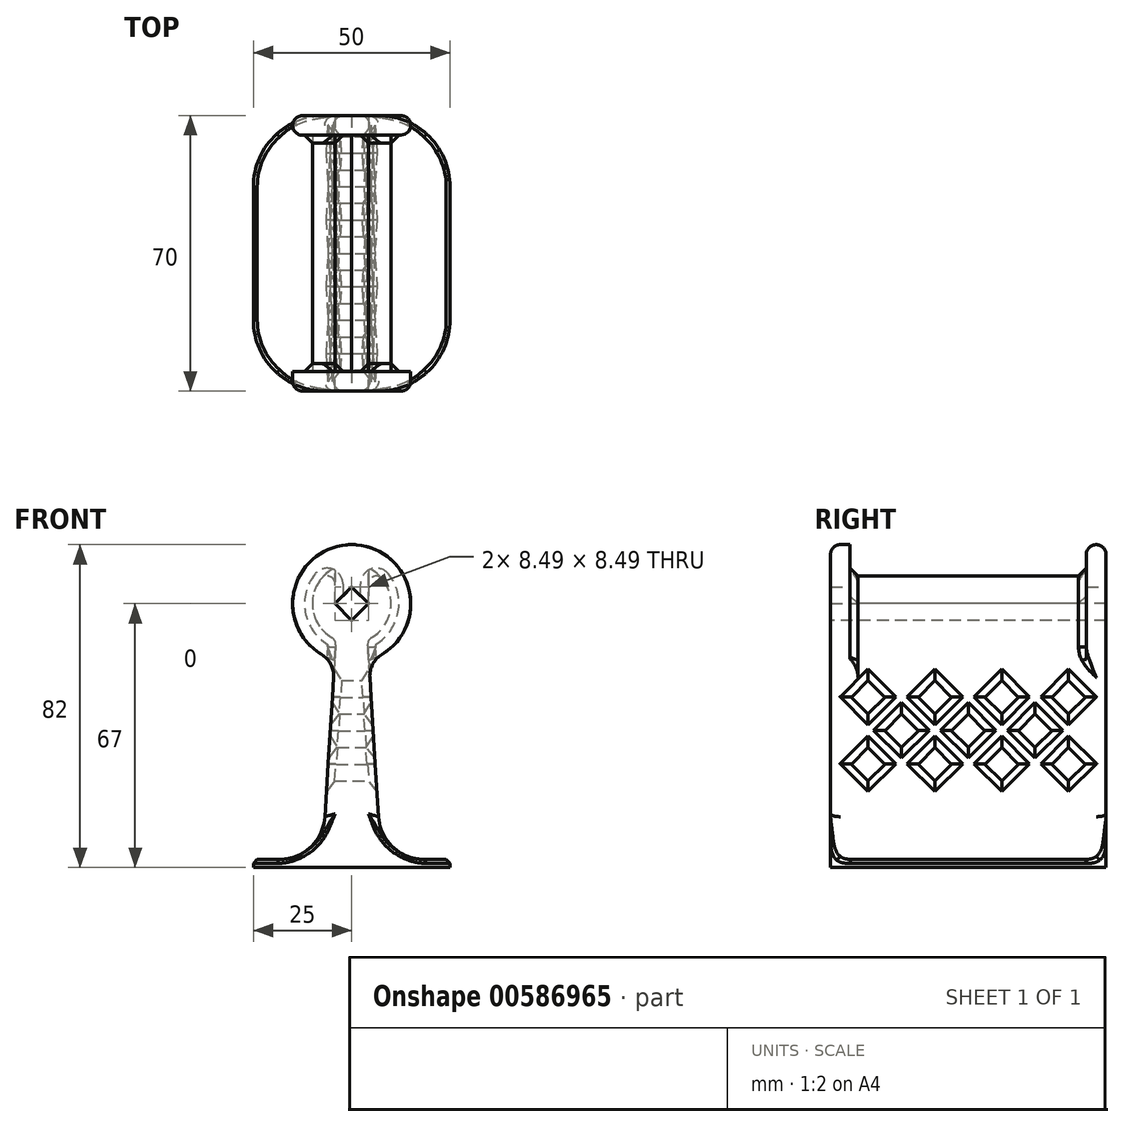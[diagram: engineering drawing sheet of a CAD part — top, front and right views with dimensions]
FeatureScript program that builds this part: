
annotation { "Feature Type Name" : "Feature", "Feature Type Description" : "" }
export const myFeature = defineFeature(function(context is Context, id is Id, definition is map)
    precondition{}
    {
        {
            var Q0;
            Q0=qCreatedBy(makeId("Front.planeOp"),FACE);
            var sketch = newSketch(context, id + "F0", { "sketchPlane" : qUnion([Q0])});
            skCircle(sketch, "E0", {"center": v(0, 0) * mm, "radius": 10 * mm});
            skCircle(sketch, "E1", {"center": v(0, 0) * mm, "radius": 15 * mm});
            skLineSegment(sketch, "E2.bottom", {"start": v(-25, -65) * mm, "end": v(25, -65) * mm});
            skLineSegment(sketch, "E2.top", {"start": v(-25, -67) * mm, "end": v(25, -67) * mm});
            skLineSegment(sketch, "E2.left", {"start": v(-25, -65) * mm, "end": v(-25, -67) * mm});
            skLineSegment(sketch, "E2.right", {"start": v(25, -65) * mm, "end": v(25, -67) * mm});
            skPoint(sketch, "E2.middle", {"position": v(0, -66) * mm});
            skLineSegment(sketch, "E3", {"start": v(-7.5, -65) * mm, "end": v(-4, -9.17) * mm});
            skLineSegment(sketch, "E4", {"start": v(7.5, -65) * mm, "end": v(4, -9.17) * mm});
            skPoint(sketch, "E5.orphan", {"position": v(-10, 0) * mm});
            skPoint(sketch, "E6.orphan", {"position": v(10, 0) * mm});
            skLineSegment(sketch, "E7", {"start": v(0, 0) * mm, "end": v(0, 10) * mm, "construction": true});
            skLineSegment(sketch, "E8", {"start": v(0, 4.24) * mm, "end": v(-4.24, 0) * mm});
            skLineSegment(sketch, "E9", {"start": v(-4.24, 0) * mm, "end": v(0, -4.24) * mm});
            skLineSegment(sketch, "E10", {"start": v(0, -4.24) * mm, "end": v(4.24, 0) * mm});
            skLineSegment(sketch, "E11", {"start": v(4.24, 0) * mm, "end": v(0, 4.24) * mm});
            skLineSegment(sketch, "E12", {"start": v(-4.24, 0) * mm, "end": v(-4.24, 9.06) * mm});
            skLineSegment(sketch, "E13", {"start": v(4.24, 0) * mm, "end": v(4.24, 9.06) * mm});
            skSolve(sketch);
        }
        {
            var Q0;
            Q0=makeQuery(id+"F0.imprint","IMPRINT",FACE,{"disambiguationData":[TD([[makeQuery(id+"F0.imprint","IMPRINT",EDGE,{"derivedFrom":sQuery(id+"F0.wireOp",EDGE,"E2.top")}),1.0]])]});
            var Q1;
            {var subQ0=sQuery(id+"F0.wireOp",EDGE,"E0");var subQ5=makeQuery(id+"F0.imprint","INTERSECT",VERTEX,{"derivedFrom":[subQ0,sQuery(id+"F0.wireOp",EDGE,"bGZqraN8-48Lf-gWye-19XN-i600Me7QwLsl")]});Q1=makeQuery(id+"F0.imprint","IMPRINT",FACE,{"disambiguationData":[TD([[makeQuery(id+"F0.imprint","IMPRINT",EDGE,{"disambiguationData":[TD([[subQ5,1.0]])],"derivedFrom":subQ0}),-1.0]])]});}
            var Q2;
            {var subQ0=sQuery(id+"F0.wireOp",EDGE,"5hKjGQrV-Ui9G-uASz-JZ0V-acZigOKFCtJ6");Q2=makeQuery(id+"F0.imprint","IMPRINT",FACE,{"disambiguationData":[TD([[makeQuery(id+"F0.imprint","IMPRINT",EDGE,{"derivedFrom":subQ0}),-1.0]])]});}
            var Q3;
            {var subQ1=sQuery(id+"F0.wireOp",EDGE,"bGZqraN8-48Lf-gWye-19XN-i600Me7QwLsl");Q3=makeQuery(id+"F0.imprint","IMPRINT",FACE,{"disambiguationData":[TD([[makeQuery(id+"F0.imprint","IMPRINT",EDGE,{"derivedFrom":subQ1}),1.0]])]});}
            var Q4;
            {var subQ0=sQuery(id+"F0.wireOp",EDGE,"bGZqraN8-48Lf-gWye-19XN-i600Me7QwLsl");Q4=makeQuery(id+"F0.imprint","IMPRINT",FACE,{"disambiguationData":[TD([[makeQuery(id+"F0.imprint","IMPRINT",EDGE,{"derivedFrom":subQ0}),-1.0]])]});}
            var Q5;
            {var subQ0=sQuery(id+"F0.wireOp",EDGE,"E3");Q5=makeQuery(id+"F0.imprint","IMPRINT",FACE,{"disambiguationData":[TD([[makeQuery(id+"F0.imprint","IMPRINT",EDGE,{"derivedFrom":subQ0}),-1.0]])]});}
            var Q6;
            {var subQ1=sQuery(id+"F0.wireOp",EDGE,"5hKjGQrV-Ui9G-uASz-JZ0V-acZigOKFCtJ6");Q6=makeQuery(id+"F0.imprint","IMPRINT",FACE,{"disambiguationData":[TD([[makeQuery(id+"F0.imprint","IMPRINT",EDGE,{"derivedFrom":subQ1}),1.0]])]});}
            var Q7;
            {var subQ0=sQuery(id+"F0.wireOp",EDGE,"FRuf11Uh-ZfHc-atdC-fj4W-Pp8RtlPbf5us");Q7=makeQuery(id+"F0.imprint","IMPRINT",FACE,{"disambiguationData":[TD([[makeQuery(id+"F0.imprint","IMPRINT",EDGE,{"derivedFrom":subQ0}),-1.0]])]});}
            var Q8;
            Q8=makeQuery(id+"F0.imprint","IMPRINT",FACE,{"disambiguationData":[TD([[makeQuery(id+"F0.imprint","IMPRINT",EDGE,{"derivedFrom":sQuery(id+"F0.wireOp",EDGE,"E8")}),-1.0]])]});
            var Q9;
            Q9=makeQuery(id+"F0.imprint","IMPRINT",FACE,{"disambiguationData":[TD([[makeQuery(id+"F0.imprint","IMPRINT",EDGE,{"derivedFrom":sQuery(id+"F0.wireOp",EDGE,"E8")}),1.0]])]});
            var Q10;
            Q10=makeQuery(id+"F0.imprint","IMPRINT",FACE,{"disambiguationData":[TD([[makeQuery(id+"F0.imprint","IMPRINT",EDGE,{"derivedFrom":sQuery(id+"F0.wireOp",EDGE,"E9")}),-1.0]])]});
            extrude(context, id + "F1", {"entities" : qUnion([Q0, Q1, Q2, Q3, Q4, Q5, Q6, Q7, Q8, Q9, Q10]), "endBound" : BoundingType.SYMMETRIC, "depth" : 70 * mm, "offsetDistance" : 25 * mm});
        }
        {
            var Q0;
            {var subQ1=sQuery(id+"F0.wireOp",EDGE,"E0");var subQ6=makeQuery(id+"F0.imprint","INTERSECT",VERTEX,{"derivedFrom":[subQ1,sQuery(id+"F0.wireOp",EDGE,"E12")]});Q0=makeQuery(id+"F0.imprint","IMPRINT",FACE,{"disambiguationData":[TD([[makeQuery(id+"F0.imprint","IMPRINT",EDGE,{"disambiguationData":[TD([[subQ6,1.0]])],"derivedFrom":subQ1}),-1.0]])]});}
            var Q1;
            Q1=makeQuery(id+"F0.imprint","IMPRINT",FACE,{"disambiguationData":[TD([[makeQuery(id+"F0.imprint","IMPRINT",EDGE,{"derivedFrom":sQuery(id+"F0.wireOp",EDGE,"E8")}),-1.0]])]});
            var Q2;
            Q2=makeQuery(id+"F0.imprint","IMPRINT",FACE,{"disambiguationData":[TD([[makeQuery(id+"F0.imprint","IMPRINT",EDGE,{"derivedFrom":sQuery(id+"F0.wireOp",EDGE,"E8")}),1.0]])]});
            extrude(context, id + "F2", {"entities" : qUnion([Q0, Q1, Q2]), "operationType" : NewBodyOperationType.REMOVE, "endBound" : BoundingType.SYMMETRIC, "oppositeDirection" : true, "depth" : 60 * mm, "offsetDistance" : 25 * mm});
        }
        {
            var Q0;
            Q0=makeQuery(id+"F0.imprint","IMPRINT",FACE,{"disambiguationData":[TD([[makeQuery(id+"F0.imprint","IMPRINT",EDGE,{"derivedFrom":sQuery(id+"F0.wireOp",EDGE,"E8")}),1.0]])]});
            extrude(context, id + "F3", {"entities" : qUnion([Q0]), "operationType" : NewBodyOperationType.REMOVE, "endBound" : BoundingType.SYMMETRIC, "depth" : 70 * mm, "offsetDistance" : 25 * mm});
        }
        {
            var Q0;
            Q0=makeQuery(id+"F1.opExtrude","CAP_EDGE",EDGE,{"disambiguationData":[OSD([sQuery(id+"F0.wireOp",EDGE,"E2.left")])],"isStart":true});
            var Q1;
            Q1=makeQuery(id+"F1.opExtrude","CAP_EDGE",EDGE,{"disambiguationData":[OSD([sQuery(id+"F0.wireOp",EDGE,"E2.left")])],"isStart":false});
            var Q2;
            Q2=makeQuery(id+"F1.opExtrude","CAP_EDGE",EDGE,{"disambiguationData":[OSD([sQuery(id+"F0.wireOp",EDGE,"E2.right")])],"isStart":true});
            var Q3;
            Q3=makeQuery(id+"F1.opExtrude","CAP_EDGE",EDGE,{"disambiguationData":[OSD([sQuery(id+"F0.wireOp",EDGE,"E2.right")])],"isStart":false});
            fillet(context, id + "F4", {"entities" : qUnion([Q0, Q1, Q2, Q3]), "radius" : 18.1 * mm, "tangentPropagation" : true, "allowEdgeOverflow" : false});
        }
        {
            var Q0;
            Q0=makeQuery(id+"F2.boolean.opBoolean","COPY",EDGE,{"derivedFrom":makeQuery(id+"F2.opExtrude","SWEPT_EDGE",EDGE,{"disambiguationData":[OSD([sQuery(id+"F0.wireOp",EDGE,"E0"),sQuery(id+"F0.wireOp",EDGE,"COAt9hvt-TYfE-I04l-2mVs-jGL3jd98xaqb")])]})});
            var Q1;
            Q1=makeQuery(id+"F2.boolean.opBoolean","COPY",EDGE,{"derivedFrom":makeQuery(id+"F2.opExtrude","SWEPT_EDGE",EDGE,{"disambiguationData":[OSD([sQuery(id+"F0.wireOp",EDGE,"E0"),sQuery(id+"F0.wireOp",EDGE,"bGZqraN8-48Lf-gWye-19XN-i600Me7QwLsl")])]})});
            var Q2;
            Q2=makeQuery(id+"F2.boolean.opBoolean","COPY",EDGE,{"derivedFrom":makeQuery(id+"F2.opExtrude","SWEPT_EDGE",EDGE,{"disambiguationData":[OSD([sQuery(id+"F0.wireOp",EDGE,"bGZqraN8-48Lf-gWye-19XN-i600Me7QwLsl"),sQuery(id+"F0.wireOp",EDGE,"COAt9hvt-TYfE-I04l-2mVs-jGL3jd98xaqb")])]})});
            fillet(context, id + "F5", {"entities" : qUnion([Q0, Q1, Q2]), "radius" : 2 * mm, "tangentPropagation" : true, "allowEdgeOverflow" : false});
        }
        {
            var Q0;
            Q0=makeQuery(id+"F2.boolean.opBoolean","COPY",EDGE,{"derivedFrom":makeQuery(id+"F2.opExtrude","SWEPT_EDGE",EDGE,{"disambiguationData":[OSD([sQuery(id+"F0.wireOp",EDGE,"E0"),sQuery(id+"F0.wireOp",EDGE,"E4")])]})});
            var Q1;
            {var subQ0=sQuery(id+"F0.wireOp",EDGE,"E4");var subQ1=sQuery(id+"F0.wireOp",EDGE,"E3");var subQ2=sQuery(id+"F0.wireOp",EDGE,"E1");Q1=makeQuery(id+"F2.boolean.opBoolean","SPLIT",EDGE,{"disambiguationData":[TD([makeQuery(id+"F2.opExtrude","CAP_FACE",FACE,{"disambiguationData":[OSD([sQuery(id+"F0.wireOp",EDGE,"E0"),subQ2,subQ1,subQ0,sQuery(id+"F0.wireOp",EDGE,"bGZqraN8-48Lf-gWye-19XN-i600Me7QwLsl"),sQuery(id+"F0.wireOp",EDGE,"COAt9hvt-TYfE-I04l-2mVs-jGL3jd98xaqb")])],"isStart":true})])],"derivedFrom":makeQuery(id+"F1.opExtrude","SWEPT_EDGE",EDGE,{"disambiguationData":[OSD([subQ2,subQ0])]})});}
            var Q2;
            {var subQ0=sQuery(id+"F0.wireOp",EDGE,"E3");var subQ1=sQuery(id+"F0.wireOp",EDGE,"E4");var subQ2=sQuery(id+"F0.wireOp",EDGE,"E1");Q2=makeQuery(id+"F2.boolean.opBoolean","SPLIT",EDGE,{"disambiguationData":[TD([makeQuery(id+"F2.opExtrude","CAP_FACE",FACE,{"disambiguationData":[OSD([sQuery(id+"F0.wireOp",EDGE,"E0"),subQ2,subQ0,subQ1,sQuery(id+"F0.wireOp",EDGE,"bGZqraN8-48Lf-gWye-19XN-i600Me7QwLsl"),sQuery(id+"F0.wireOp",EDGE,"COAt9hvt-TYfE-I04l-2mVs-jGL3jd98xaqb")])],"isStart":true})])],"derivedFrom":makeQuery(id+"F1.opExtrude","SWEPT_EDGE",EDGE,{"disambiguationData":[OSD([subQ2,subQ0])]})});}
            var Q3;
            Q3=makeQuery(id+"F2.boolean.opBoolean","COPY",EDGE,{"derivedFrom":makeQuery(id+"F2.opExtrude","SWEPT_EDGE",EDGE,{"disambiguationData":[OSD([sQuery(id+"F0.wireOp",EDGE,"E0"),sQuery(id+"F0.wireOp",EDGE,"E3")])]})});
            var Q4;
            {var subQ0=sQuery(id+"F0.wireOp",EDGE,"E4");var subQ1=sQuery(id+"F0.wireOp",EDGE,"E3");var subQ2=sQuery(id+"F0.wireOp",EDGE,"E1");Q4=makeQuery(id+"F2.boolean.opBoolean","SPLIT",EDGE,{"disambiguationData":[TD([makeQuery(id+"F2.opExtrude","CAP_FACE",FACE,{"disambiguationData":[OSD([sQuery(id+"F0.wireOp",EDGE,"E0"),subQ2,subQ1,subQ0,sQuery(id+"F0.wireOp",EDGE,"bGZqraN8-48Lf-gWye-19XN-i600Me7QwLsl"),sQuery(id+"F0.wireOp",EDGE,"COAt9hvt-TYfE-I04l-2mVs-jGL3jd98xaqb")])],"isStart":false})])],"derivedFrom":makeQuery(id+"F1.opExtrude","SWEPT_EDGE",EDGE,{"disambiguationData":[OSD([subQ2,subQ0])]})});}
            var Q5;
            {var subQ0=sQuery(id+"F0.wireOp",EDGE,"E4");var subQ1=sQuery(id+"F0.wireOp",EDGE,"E3");var subQ2=sQuery(id+"F0.wireOp",EDGE,"E1");Q5=makeQuery(id+"F2.boolean.opBoolean","SPLIT",EDGE,{"disambiguationData":[TD([makeQuery(id+"F2.opExtrude","CAP_FACE",FACE,{"disambiguationData":[OSD([sQuery(id+"F0.wireOp",EDGE,"E0"),subQ2,subQ1,subQ0,sQuery(id+"F0.wireOp",EDGE,"bGZqraN8-48Lf-gWye-19XN-i600Me7QwLsl"),sQuery(id+"F0.wireOp",EDGE,"COAt9hvt-TYfE-I04l-2mVs-jGL3jd98xaqb")])],"isStart":false})])],"derivedFrom":makeQuery(id+"F1.opExtrude","SWEPT_EDGE",EDGE,{"disambiguationData":[OSD([subQ2,subQ1])]})});}
            fillet(context, id + "F6", {"entities" : qUnion([Q0, Q1, Q2, Q3, Q4, Q5]), "radius" : 6.43 * mm, "tangentPropagation" : true, "allowEdgeOverflow" : false});
        }
        {
            var Q0;
            Q0=makeQuery(id+"F1.opExtrude","CAP_EDGE",EDGE,{"disambiguationData":[OSD([sQuery(id+"F0.wireOp",EDGE,"E1")])],"isStart":false});
            var Q1;
            Q1=makeQuery(id+"F1.opExtrude","CAP_EDGE",EDGE,{"disambiguationData":[OSD([sQuery(id+"F0.wireOp",EDGE,"E1")])],"isStart":true});
            var Q2;
            Q2=makeQuery(id+"F2.boolean.opBoolean","COPY",EDGE,{"derivedFrom":makeQuery(id+"F2.opExtrude","CAP_EDGE",EDGE,{"disambiguationData":[OSD([sQuery(id+"F0.wireOp",EDGE,"E1")])],"isStart":false})});
            var Q3;
            Q3=makeQuery(id+"F2.boolean.opBoolean","COPY",EDGE,{"derivedFrom":makeQuery(id+"F2.opExtrude","CAP_EDGE",EDGE,{"disambiguationData":[OSD([sQuery(id+"F0.wireOp",EDGE,"E1")])],"isStart":true})});
            fillet(context, id + "F7", {"entities" : qUnion([Q0, Q1, Q2, Q3]), "radius" : 2.5 * mm, "tangentPropagation" : true, "allowEdgeOverflow" : false});
        }
        {
            var Q0;
            Q0=makeQuery(id+"F1.opExtrude","SWEPT_EDGE",EDGE,{"disambiguationData":[OSD([sQuery(id+"F0.wireOp",EDGE,"E2.bottom"),sQuery(id+"F0.wireOp",EDGE,"E3")])]});
            var Q1;
            Q1=makeQuery(id+"F1.opExtrude","SWEPT_EDGE",EDGE,{"disambiguationData":[OSD([sQuery(id+"F0.wireOp",EDGE,"E2.bottom"),sQuery(id+"F0.wireOp",EDGE,"E4")])]});
            fillet(context, id + "F8", {"entities" : qUnion([Q0, Q1]), "radius" : 11.6 * mm, "tangentPropagation" : true, "allowEdgeOverflow" : false});
        }
        {
            var Q0;
            Q0=makeQuery(id+"F1.opExtrude","SWEPT_EDGE",EDGE,{"disambiguationData":[OSD([sQuery(id+"F0.wireOp",EDGE,"E2.bottom"),sQuery(id+"F0.wireOp",EDGE,"E2.right")])]});
            var Q1;
            Q1=makeQuery(id+"F1.opExtrude","SWEPT_EDGE",EDGE,{"disambiguationData":[OSD([sQuery(id+"F0.wireOp",EDGE,"E2.bottom"),sQuery(id+"F0.wireOp",EDGE,"E2.left")])]});
            chamfer(context, id + "F9", {"entities" : qUnion([Q0, Q1]), "width" : 1 * mm, "tangentPropagation" : true});
        }
        {
            var Q0;
            Q0=qCreatedBy(makeId("Right.planeOp"),FACE);
            var sketch = newSketch(context, id + "F10", { "sketchPlane" : qUnion([Q0])});
            skLineSegment(sketch, "E14", {"start": v(-25.46, -36.55) * mm, "end": v(-29.7, -40.79) * mm});
            skLineSegment(sketch, "E15", {"start": v(-29.7, -40.79) * mm, "end": v(-25.46, -45.03) * mm});
            skLineSegment(sketch, "E16", {"start": v(-25.46, -45.03) * mm, "end": v(-21.21, -40.79) * mm});
            skLineSegment(sketch, "E17", {"start": v(-21.21, -40.79) * mm, "end": v(-25.46, -36.55) * mm});
            skLineSegment(sketch, "E18.0.1.0", {"start": v(-21.21, -23.82) * mm, "end": v(-25.46, -19.58) * mm});
            skLineSegment(sketch, "E18.0.1.1", {"start": v(-25.46, -19.58) * mm, "end": v(-29.7, -23.82) * mm});
            skLineSegment(sketch, "E18.0.1.2", {"start": v(-29.7, -23.82) * mm, "end": v(-25.46, -28.06) * mm});
            skLineSegment(sketch, "E18.0.1.3", {"start": v(-25.46, -28.06) * mm, "end": v(-21.21, -23.82) * mm});
            skLineSegment(sketch, "E18.1.0.0", {"start": v(-12.73, -49.27) * mm, "end": v(-16.97, -45.03) * mm});
            skLineSegment(sketch, "E18.1.0.1", {"start": v(-16.97, -45.03) * mm, "end": v(-21.21, -49.27) * mm});
            skLineSegment(sketch, "E18.1.0.2", {"start": v(-21.21, -49.27) * mm, "end": v(-16.97, -53.52) * mm});
            skLineSegment(sketch, "E18.1.0.3", {"start": v(-16.97, -53.52) * mm, "end": v(-12.73, -49.27) * mm});
            skLineSegment(sketch, "E18.1.1.0", {"start": v(-12.73, -32.3) * mm, "end": v(-16.97, -28.06) * mm});
            skLineSegment(sketch, "E18.1.1.1", {"start": v(-16.97, -28.06) * mm, "end": v(-21.21, -32.3) * mm});
            skLineSegment(sketch, "E18.1.1.2", {"start": v(-21.21, -32.3) * mm, "end": v(-16.97, -36.55) * mm});
            skLineSegment(sketch, "E18.1.1.3", {"start": v(-16.97, -36.55) * mm, "end": v(-12.73, -32.3) * mm});
            skLineSegment(sketch, "E18.2.0.0", {"start": v(-4.24, -57.76) * mm, "end": v(-8.49, -53.52) * mm});
            skLineSegment(sketch, "E18.2.0.1", {"start": v(-8.49, -53.52) * mm, "end": v(-12.73, -57.76) * mm});
            skLineSegment(sketch, "E18.2.0.2", {"start": v(-12.73, -57.76) * mm, "end": v(-8.49, -62) * mm});
            skLineSegment(sketch, "E18.2.0.3", {"start": v(-8.49, -62) * mm, "end": v(-4.24, -57.76) * mm});
            skLineSegment(sketch, "E18.2.1.0", {"start": v(-4.24, -40.79) * mm, "end": v(-8.49, -36.55) * mm});
            skLineSegment(sketch, "E18.2.1.1", {"start": v(-8.49, -36.55) * mm, "end": v(-12.73, -40.79) * mm});
            skLineSegment(sketch, "E18.2.1.2", {"start": v(-12.73, -40.79) * mm, "end": v(-8.49, -45.03) * mm});
            skLineSegment(sketch, "E18.2.1.3", {"start": v(-8.49, -45.03) * mm, "end": v(-4.24, -40.79) * mm});
            skLineSegment(sketch, "E18.direction1", {"start": v(-29.7, -40.79) * mm, "end": v(-21.21, -49.27) * mm, "construction": true});
            skLineSegment(sketch, "E18.direction2", {"start": v(-29.7, -40.79) * mm, "end": v(-29.7, -23.82) * mm, "construction": true});
            skLineSegment(sketch, "E19.0.3.0", {"start": v(4.24, -66.25) * mm, "end": v(0, -62) * mm});
            skLineSegment(sketch, "E19.3.3.0", {"start": v(0, -62) * mm, "end": v(-4.24, -66.25) * mm});
            skLineSegment(sketch, "E19.6.3.0", {"start": v(-4.24, -66.25) * mm, "end": v(0, -70.49) * mm});
            skLineSegment(sketch, "E19.9.3.0", {"start": v(0, -70.49) * mm, "end": v(4.24, -66.25) * mm});
            skLineSegment(sketch, "E19.0.3.1", {"start": v(4.24, -49.27) * mm, "end": v(0, -45.03) * mm});
            skLineSegment(sketch, "E19.3.3.1", {"start": v(0, -45.03) * mm, "end": v(-4.24, -49.27) * mm});
            skLineSegment(sketch, "E19.6.3.1", {"start": v(-4.24, -49.27) * mm, "end": v(0, -53.52) * mm});
            skLineSegment(sketch, "E19.9.3.1", {"start": v(0, -53.52) * mm, "end": v(4.24, -49.27) * mm});
            skLineSegment(sketch, "E20.0.0.2", {"start": v(-21.21, -6.85) * mm, "end": v(-25.46, -2.6) * mm});
            skLineSegment(sketch, "E20.3.0.2", {"start": v(-25.46, -2.6) * mm, "end": v(-29.7, -6.85) * mm});
            skLineSegment(sketch, "E20.6.0.2", {"start": v(-29.7, -6.85) * mm, "end": v(-25.46, -11.1) * mm});
            skLineSegment(sketch, "E20.9.0.2", {"start": v(-25.46, -11.1) * mm, "end": v(-21.21, -6.85) * mm});
            skLineSegment(sketch, "E20.0.0.3", {"start": v(-21.21, 10.12) * mm, "end": v(-25.46, 14.36) * mm});
            skLineSegment(sketch, "E20.3.0.3", {"start": v(-25.46, 14.36) * mm, "end": v(-29.7, 10.12) * mm});
            skLineSegment(sketch, "E20.6.0.3", {"start": v(-29.7, 10.12) * mm, "end": v(-25.46, 5.88) * mm});
            skLineSegment(sketch, "E20.9.0.3", {"start": v(-25.46, 5.88) * mm, "end": v(-21.21, 10.12) * mm});
            skLineSegment(sketch, "E20.0.0.4", {"start": v(-21.21, 27.1) * mm, "end": v(-25.46, 31.34) * mm});
            skLineSegment(sketch, "E20.3.0.4", {"start": v(-25.46, 31.34) * mm, "end": v(-29.7, 27.1) * mm});
            skLineSegment(sketch, "E20.6.0.4", {"start": v(-29.7, 27.1) * mm, "end": v(-25.46, 22.85) * mm});
            skLineSegment(sketch, "E20.9.0.4", {"start": v(-25.46, 22.85) * mm, "end": v(-21.21, 27.1) * mm});
            skLineSegment(sketch, "E20.0.0.5", {"start": v(-21.21, 44.06) * mm, "end": v(-25.46, 48.3) * mm});
            skLineSegment(sketch, "E20.3.0.5", {"start": v(-25.46, 48.3) * mm, "end": v(-29.7, 44.06) * mm});
            skLineSegment(sketch, "E20.6.0.5", {"start": v(-29.7, 44.06) * mm, "end": v(-25.46, 39.82) * mm});
            skLineSegment(sketch, "E20.9.0.5", {"start": v(-25.46, 39.82) * mm, "end": v(-21.21, 44.06) * mm});
            skLineSegment(sketch, "E20.0.1.2", {"start": v(-12.73, -15.33) * mm, "end": v(-16.97, -11.1) * mm});
            skLineSegment(sketch, "E20.3.1.2", {"start": v(-16.97, -11.1) * mm, "end": v(-21.21, -15.33) * mm});
            skLineSegment(sketch, "E20.6.1.2", {"start": v(-21.21, -15.33) * mm, "end": v(-16.97, -19.58) * mm});
            skLineSegment(sketch, "E20.9.1.2", {"start": v(-16.97, -19.58) * mm, "end": v(-12.73, -15.33) * mm});
            skLineSegment(sketch, "E20.0.1.3", {"start": v(-12.73, 1.64) * mm, "end": v(-16.97, 5.88) * mm});
            skLineSegment(sketch, "E20.3.1.3", {"start": v(-16.97, 5.88) * mm, "end": v(-21.21, 1.64) * mm});
            skLineSegment(sketch, "E20.6.1.3", {"start": v(-21.21, 1.64) * mm, "end": v(-16.97, -2.6) * mm});
            skLineSegment(sketch, "E20.9.1.3", {"start": v(-16.97, -2.6) * mm, "end": v(-12.73, 1.64) * mm});
            skLineSegment(sketch, "E20.0.1.4", {"start": v(-12.73, 18.6) * mm, "end": v(-16.97, 22.85) * mm});
            skLineSegment(sketch, "E20.3.1.4", {"start": v(-16.97, 22.85) * mm, "end": v(-21.21, 18.6) * mm});
            skLineSegment(sketch, "E20.6.1.4", {"start": v(-21.21, 18.6) * mm, "end": v(-16.97, 14.36) * mm});
            skLineSegment(sketch, "E20.9.1.4", {"start": v(-16.97, 14.36) * mm, "end": v(-12.73, 18.6) * mm});
            skLineSegment(sketch, "E20.0.1.5", {"start": v(-12.73, 35.58) * mm, "end": v(-16.97, 39.82) * mm});
            skLineSegment(sketch, "E20.3.1.5", {"start": v(-16.97, 39.82) * mm, "end": v(-21.21, 35.58) * mm});
            skLineSegment(sketch, "E20.6.1.5", {"start": v(-21.21, 35.58) * mm, "end": v(-16.97, 31.34) * mm});
            skLineSegment(sketch, "E20.9.1.5", {"start": v(-16.97, 31.34) * mm, "end": v(-12.73, 35.58) * mm});
            skLineSegment(sketch, "E20.0.2.2", {"start": v(-4.24, -23.82) * mm, "end": v(-8.49, -19.58) * mm});
            skLineSegment(sketch, "E20.3.2.2", {"start": v(-8.49, -19.58) * mm, "end": v(-12.73, -23.82) * mm});
            skLineSegment(sketch, "E20.6.2.2", {"start": v(-12.73, -23.82) * mm, "end": v(-8.49, -28.06) * mm});
            skLineSegment(sketch, "E20.9.2.2", {"start": v(-8.49, -28.06) * mm, "end": v(-4.24, -23.82) * mm});
            skLineSegment(sketch, "E20.0.2.3", {"start": v(-4.24, -6.85) * mm, "end": v(-8.49, -2.6) * mm});
            skLineSegment(sketch, "E20.3.2.3", {"start": v(-8.49, -2.6) * mm, "end": v(-12.73, -6.85) * mm});
            skLineSegment(sketch, "E20.6.2.3", {"start": v(-12.73, -6.85) * mm, "end": v(-8.49, -11.1) * mm});
            skLineSegment(sketch, "E20.9.2.3", {"start": v(-8.49, -11.1) * mm, "end": v(-4.24, -6.85) * mm});
            skLineSegment(sketch, "E20.0.2.4", {"start": v(-4.24, 10.12) * mm, "end": v(-8.49, 14.36) * mm});
            skLineSegment(sketch, "E20.3.2.4", {"start": v(-8.49, 14.36) * mm, "end": v(-12.73, 10.12) * mm});
            skLineSegment(sketch, "E20.6.2.4", {"start": v(-12.73, 10.12) * mm, "end": v(-8.49, 5.88) * mm});
            skLineSegment(sketch, "E20.9.2.4", {"start": v(-8.49, 5.88) * mm, "end": v(-4.24, 10.12) * mm});
            skLineSegment(sketch, "E20.0.2.5", {"start": v(-4.24, 27.1) * mm, "end": v(-8.49, 31.34) * mm});
            skLineSegment(sketch, "E20.3.2.5", {"start": v(-8.49, 31.34) * mm, "end": v(-12.73, 27.1) * mm});
            skLineSegment(sketch, "E20.6.2.5", {"start": v(-12.73, 27.1) * mm, "end": v(-8.49, 22.85) * mm});
            skLineSegment(sketch, "E20.9.2.5", {"start": v(-8.49, 22.85) * mm, "end": v(-4.24, 27.1) * mm});
            skLineSegment(sketch, "E20.0.3.2", {"start": v(4.24, -32.3) * mm, "end": v(0, -28.06) * mm});
            skLineSegment(sketch, "E20.3.3.2", {"start": v(0, -28.06) * mm, "end": v(-4.24, -32.3) * mm});
            skLineSegment(sketch, "E20.6.3.2", {"start": v(-4.24, -32.3) * mm, "end": v(0, -36.55) * mm});
            skLineSegment(sketch, "E20.9.3.2", {"start": v(0, -36.55) * mm, "end": v(4.24, -32.3) * mm});
            skLineSegment(sketch, "E20.0.3.3", {"start": v(4.24, -15.33) * mm, "end": v(0, -11.1) * mm});
            skLineSegment(sketch, "E20.3.3.3", {"start": v(0, -11.1) * mm, "end": v(-4.24, -15.33) * mm});
            skLineSegment(sketch, "E20.6.3.3", {"start": v(-4.24, -15.33) * mm, "end": v(0, -19.58) * mm});
            skLineSegment(sketch, "E20.9.3.3", {"start": v(0, -19.58) * mm, "end": v(4.24, -15.33) * mm});
            skLineSegment(sketch, "E20.0.3.4", {"start": v(4.24, 1.64) * mm, "end": v(0, 5.88) * mm});
            skLineSegment(sketch, "E20.3.3.4", {"start": v(0, 5.88) * mm, "end": v(-4.24, 1.64) * mm});
            skLineSegment(sketch, "E20.6.3.4", {"start": v(-4.24, 1.64) * mm, "end": v(0, -2.6) * mm});
            skLineSegment(sketch, "E20.9.3.4", {"start": v(0, -2.6) * mm, "end": v(4.24, 1.64) * mm});
            skLineSegment(sketch, "E20.0.3.5", {"start": v(4.24, 18.6) * mm, "end": v(0, 22.85) * mm});
            skLineSegment(sketch, "E20.3.3.5", {"start": v(0, 22.85) * mm, "end": v(-4.24, 18.6) * mm});
            skLineSegment(sketch, "E20.6.3.5", {"start": v(-4.24, 18.6) * mm, "end": v(0, 14.36) * mm});
            skLineSegment(sketch, "E20.9.3.5", {"start": v(0, 14.36) * mm, "end": v(4.24, 18.6) * mm});
            skLineSegment(sketch, "E21.0.4.0", {"start": v(12.73, -74.73) * mm, "end": v(8.49, -70.49) * mm});
            skLineSegment(sketch, "E21.3.4.0", {"start": v(8.49, -70.49) * mm, "end": v(4.24, -74.73) * mm});
            skLineSegment(sketch, "E21.6.4.0", {"start": v(4.24, -74.73) * mm, "end": v(8.49, -78.97) * mm});
            skLineSegment(sketch, "E21.9.4.0", {"start": v(8.49, -78.97) * mm, "end": v(12.73, -74.73) * mm});
            skLineSegment(sketch, "E21.0.4.1", {"start": v(12.73, -57.76) * mm, "end": v(8.49, -53.52) * mm});
            skLineSegment(sketch, "E21.3.4.1", {"start": v(8.49, -53.52) * mm, "end": v(4.24, -57.76) * mm});
            skLineSegment(sketch, "E21.6.4.1", {"start": v(4.24, -57.76) * mm, "end": v(8.49, -62) * mm});
            skLineSegment(sketch, "E21.9.4.1", {"start": v(8.49, -62) * mm, "end": v(12.73, -57.76) * mm});
            skLineSegment(sketch, "E21.0.4.2", {"start": v(12.73, -40.79) * mm, "end": v(8.49, -36.55) * mm});
            skLineSegment(sketch, "E21.3.4.2", {"start": v(8.49, -36.55) * mm, "end": v(4.24, -40.79) * mm});
            skLineSegment(sketch, "E21.6.4.2", {"start": v(4.24, -40.79) * mm, "end": v(8.49, -45.03) * mm});
            skLineSegment(sketch, "E21.9.4.2", {"start": v(8.49, -45.03) * mm, "end": v(12.73, -40.79) * mm});
            skLineSegment(sketch, "E21.0.4.3", {"start": v(12.73, -23.82) * mm, "end": v(8.49, -19.58) * mm});
            skLineSegment(sketch, "E21.3.4.3", {"start": v(8.49, -19.58) * mm, "end": v(4.24, -23.82) * mm});
            skLineSegment(sketch, "E21.6.4.3", {"start": v(4.24, -23.82) * mm, "end": v(8.49, -28.06) * mm});
            skLineSegment(sketch, "E21.9.4.3", {"start": v(8.49, -28.06) * mm, "end": v(12.73, -23.82) * mm});
            skLineSegment(sketch, "E21.0.4.4", {"start": v(12.73, -6.85) * mm, "end": v(8.49, -2.6) * mm});
            skLineSegment(sketch, "E21.3.4.4", {"start": v(8.49, -2.6) * mm, "end": v(4.24, -6.85) * mm});
            skLineSegment(sketch, "E21.6.4.4", {"start": v(4.24, -6.85) * mm, "end": v(8.49, -11.1) * mm});
            skLineSegment(sketch, "E21.9.4.4", {"start": v(8.49, -11.1) * mm, "end": v(12.73, -6.85) * mm});
            skLineSegment(sketch, "E21.0.4.5", {"start": v(12.73, 10.12) * mm, "end": v(8.49, 14.36) * mm});
            skLineSegment(sketch, "E21.3.4.5", {"start": v(8.49, 14.36) * mm, "end": v(4.24, 10.12) * mm});
            skLineSegment(sketch, "E21.6.4.5", {"start": v(4.24, 10.12) * mm, "end": v(8.49, 5.88) * mm});
            skLineSegment(sketch, "E21.9.4.5", {"start": v(8.49, 5.88) * mm, "end": v(12.73, 10.12) * mm});
            skLineSegment(sketch, "E21.0.5.0", {"start": v(21.21, -83.22) * mm, "end": v(16.97, -78.97) * mm});
            skLineSegment(sketch, "E21.3.5.0", {"start": v(16.97, -78.97) * mm, "end": v(12.73, -83.22) * mm});
            skLineSegment(sketch, "E21.6.5.0", {"start": v(12.73, -83.22) * mm, "end": v(16.97, -87.46) * mm});
            skLineSegment(sketch, "E21.9.5.0", {"start": v(16.97, -87.46) * mm, "end": v(21.21, -83.22) * mm});
            skLineSegment(sketch, "E21.0.5.1", {"start": v(21.21, -66.25) * mm, "end": v(16.97, -62) * mm});
            skLineSegment(sketch, "E21.3.5.1", {"start": v(16.97, -62) * mm, "end": v(12.73, -66.25) * mm});
            skLineSegment(sketch, "E21.6.5.1", {"start": v(12.73, -66.25) * mm, "end": v(16.97, -70.49) * mm});
            skLineSegment(sketch, "E21.9.5.1", {"start": v(16.97, -70.49) * mm, "end": v(21.21, -66.25) * mm});
            skLineSegment(sketch, "E21.0.5.2", {"start": v(21.21, -49.27) * mm, "end": v(16.97, -45.03) * mm});
            skLineSegment(sketch, "E21.3.5.2", {"start": v(16.97, -45.03) * mm, "end": v(12.73, -49.27) * mm});
            skLineSegment(sketch, "E21.6.5.2", {"start": v(12.73, -49.27) * mm, "end": v(16.97, -53.52) * mm});
            skLineSegment(sketch, "E21.9.5.2", {"start": v(16.97, -53.52) * mm, "end": v(21.21, -49.27) * mm});
            skLineSegment(sketch, "E21.0.5.3", {"start": v(21.21, -32.3) * mm, "end": v(16.97, -28.06) * mm});
            skLineSegment(sketch, "E21.3.5.3", {"start": v(16.97, -28.06) * mm, "end": v(12.73, -32.3) * mm});
            skLineSegment(sketch, "E21.6.5.3", {"start": v(12.73, -32.3) * mm, "end": v(16.97, -36.55) * mm});
            skLineSegment(sketch, "E21.9.5.3", {"start": v(16.97, -36.55) * mm, "end": v(21.21, -32.3) * mm});
            skLineSegment(sketch, "E21.0.5.4", {"start": v(21.21, -15.33) * mm, "end": v(16.97, -11.1) * mm});
            skLineSegment(sketch, "E21.3.5.4", {"start": v(16.97, -11.1) * mm, "end": v(12.73, -15.33) * mm});
            skLineSegment(sketch, "E21.6.5.4", {"start": v(12.73, -15.33) * mm, "end": v(16.97, -19.58) * mm});
            skLineSegment(sketch, "E21.9.5.4", {"start": v(16.97, -19.58) * mm, "end": v(21.21, -15.33) * mm});
            skLineSegment(sketch, "E21.0.5.5", {"start": v(21.21, 1.64) * mm, "end": v(16.97, 5.88) * mm});
            skLineSegment(sketch, "E21.3.5.5", {"start": v(16.97, 5.88) * mm, "end": v(12.73, 1.64) * mm});
            skLineSegment(sketch, "E21.6.5.5", {"start": v(12.73, 1.64) * mm, "end": v(16.97, -2.6) * mm});
            skLineSegment(sketch, "E21.9.5.5", {"start": v(16.97, -2.6) * mm, "end": v(21.21, 1.64) * mm});
            skLineSegment(sketch, "E21.0.6.0", {"start": v(29.7, -91.7) * mm, "end": v(25.46, -87.46) * mm});
            skLineSegment(sketch, "E21.3.6.0", {"start": v(25.46, -87.46) * mm, "end": v(21.21, -91.7) * mm});
            skLineSegment(sketch, "E21.6.6.0", {"start": v(21.21, -91.7) * mm, "end": v(25.46, -95.94) * mm});
            skLineSegment(sketch, "E21.9.6.0", {"start": v(25.46, -95.94) * mm, "end": v(29.7, -91.7) * mm});
            skLineSegment(sketch, "E21.0.6.1", {"start": v(29.7, -74.73) * mm, "end": v(25.46, -70.49) * mm});
            skLineSegment(sketch, "E21.3.6.1", {"start": v(25.46, -70.49) * mm, "end": v(21.21, -74.73) * mm});
            skLineSegment(sketch, "E21.6.6.1", {"start": v(21.21, -74.73) * mm, "end": v(25.46, -78.97) * mm});
            skLineSegment(sketch, "E21.9.6.1", {"start": v(25.46, -78.97) * mm, "end": v(29.7, -74.73) * mm});
            skLineSegment(sketch, "E21.0.6.2", {"start": v(29.7, -57.76) * mm, "end": v(25.46, -53.52) * mm});
            skLineSegment(sketch, "E21.3.6.2", {"start": v(25.46, -53.52) * mm, "end": v(21.21, -57.76) * mm});
            skLineSegment(sketch, "E21.6.6.2", {"start": v(21.21, -57.76) * mm, "end": v(25.46, -62) * mm});
            skLineSegment(sketch, "E21.9.6.2", {"start": v(25.46, -62) * mm, "end": v(29.7, -57.76) * mm});
            skLineSegment(sketch, "E21.0.6.3", {"start": v(29.7, -40.79) * mm, "end": v(25.46, -36.55) * mm});
            skLineSegment(sketch, "E21.3.6.3", {"start": v(25.46, -36.55) * mm, "end": v(21.21, -40.79) * mm});
            skLineSegment(sketch, "E21.6.6.3", {"start": v(21.21, -40.79) * mm, "end": v(25.46, -45.03) * mm});
            skLineSegment(sketch, "E21.9.6.3", {"start": v(25.46, -45.03) * mm, "end": v(29.7, -40.79) * mm});
            skLineSegment(sketch, "E21.0.6.4", {"start": v(29.7, -23.82) * mm, "end": v(25.46, -19.58) * mm});
            skLineSegment(sketch, "E21.3.6.4", {"start": v(25.46, -19.58) * mm, "end": v(21.21, -23.82) * mm});
            skLineSegment(sketch, "E21.6.6.4", {"start": v(21.21, -23.82) * mm, "end": v(25.46, -28.06) * mm});
            skLineSegment(sketch, "E21.9.6.4", {"start": v(25.46, -28.06) * mm, "end": v(29.7, -23.82) * mm});
            skLineSegment(sketch, "E21.0.6.5", {"start": v(29.7, -6.85) * mm, "end": v(25.46, -2.6) * mm});
            skLineSegment(sketch, "E21.3.6.5", {"start": v(25.46, -2.6) * mm, "end": v(21.21, -6.85) * mm});
            skLineSegment(sketch, "E21.6.6.5", {"start": v(21.21, -6.85) * mm, "end": v(25.46, -11.1) * mm});
            skLineSegment(sketch, "E21.9.6.5", {"start": v(25.46, -11.1) * mm, "end": v(29.7, -6.85) * mm});
            skLineSegment(sketch, "E21.0.7.0", {"start": v(38.18, -100.19) * mm, "end": v(33.94, -95.94) * mm});
            skLineSegment(sketch, "E21.3.7.0", {"start": v(33.94, -95.94) * mm, "end": v(29.7, -100.19) * mm});
            skLineSegment(sketch, "E21.6.7.0", {"start": v(29.7, -100.19) * mm, "end": v(33.94, -104.43) * mm});
            skLineSegment(sketch, "E21.9.7.0", {"start": v(33.94, -104.43) * mm, "end": v(38.18, -100.19) * mm});
            skLineSegment(sketch, "E21.0.7.1", {"start": v(38.18, -83.22) * mm, "end": v(33.94, -78.97) * mm});
            skLineSegment(sketch, "E21.3.7.1", {"start": v(33.94, -78.97) * mm, "end": v(29.7, -83.22) * mm});
            skLineSegment(sketch, "E21.6.7.1", {"start": v(29.7, -83.22) * mm, "end": v(33.94, -87.46) * mm});
            skLineSegment(sketch, "E21.9.7.1", {"start": v(33.94, -87.46) * mm, "end": v(38.18, -83.22) * mm});
            skLineSegment(sketch, "E21.0.7.2", {"start": v(38.18, -66.25) * mm, "end": v(33.94, -62) * mm});
            skLineSegment(sketch, "E21.3.7.2", {"start": v(33.94, -62) * mm, "end": v(29.7, -66.25) * mm});
            skLineSegment(sketch, "E21.6.7.2", {"start": v(29.7, -66.25) * mm, "end": v(33.94, -70.49) * mm});
            skLineSegment(sketch, "E21.9.7.2", {"start": v(33.94, -70.49) * mm, "end": v(38.18, -66.25) * mm});
            skLineSegment(sketch, "E21.0.7.3", {"start": v(38.18, -49.27) * mm, "end": v(33.94, -45.03) * mm});
            skLineSegment(sketch, "E21.3.7.3", {"start": v(33.94, -45.03) * mm, "end": v(29.7, -49.27) * mm});
            skLineSegment(sketch, "E21.6.7.3", {"start": v(29.7, -49.27) * mm, "end": v(33.94, -53.52) * mm});
            skLineSegment(sketch, "E21.9.7.3", {"start": v(33.94, -53.52) * mm, "end": v(38.18, -49.27) * mm});
            skLineSegment(sketch, "E21.0.7.4", {"start": v(38.18, -32.3) * mm, "end": v(33.94, -28.06) * mm});
            skLineSegment(sketch, "E21.3.7.4", {"start": v(33.94, -28.06) * mm, "end": v(29.7, -32.3) * mm});
            skLineSegment(sketch, "E21.6.7.4", {"start": v(29.7, -32.3) * mm, "end": v(33.94, -36.55) * mm});
            skLineSegment(sketch, "E21.9.7.4", {"start": v(33.94, -36.55) * mm, "end": v(38.18, -32.3) * mm});
            skLineSegment(sketch, "E21.0.7.5", {"start": v(38.18, -15.33) * mm, "end": v(33.94, -11.1) * mm});
            skLineSegment(sketch, "E21.3.7.5", {"start": v(33.94, -11.1) * mm, "end": v(29.7, -15.33) * mm});
            skLineSegment(sketch, "E21.6.7.5", {"start": v(29.7, -15.33) * mm, "end": v(33.94, -19.58) * mm});
            skLineSegment(sketch, "E21.9.7.5", {"start": v(33.94, -19.58) * mm, "end": v(38.18, -15.33) * mm});
            skLineSegment(sketch, "E22", {"start": v(-21.21, -40.79) * mm, "end": v(-16.97, -36.55) * mm, "construction": true});
            skLineSegment(sketch, "E23", {"start": v(-16.97, -45.03) * mm, "end": v(-21.21, -40.79) * mm, "construction": true});
            skLineSegment(sketch, "E24", {"start": v(29.7, -40.79) * mm, "end": v(32.5, -40.79) * mm, "construction": true});
            skLineSegment(sketch, "E25", {"start": v(-29.7, -40.79) * mm, "end": v(-32.5, -40.79) * mm, "construction": true});
            skLineSegment(sketch, "E26", {"start": v(-25.46, -45.03) * mm, "end": v(-25.46, -54.14) * mm, "construction": true});
            skLineSegment(sketch, "E27", {"start": v(-25.46, -19.58) * mm, "end": v(-25.46, -10.47) * mm, "construction": true});
            skSolve(sketch);
        }
        {
            var Q0;
            Q0=makeQuery(id+"F10.imprint","IMPRINT",FACE,{"disambiguationData":[TD([[makeQuery(id+"F10.imprint","IMPRINT",EDGE,{"derivedFrom":sQuery(id+"F10.wireOp",EDGE,"E14")}),1.0]])]});
            var Q1;
            Q1=makeQuery(id+"F10.imprint","IMPRINT",FACE,{"disambiguationData":[TD([[makeQuery(id+"F10.imprint","IMPRINT",EDGE,{"derivedFrom":sQuery(id+"F10.wireOp",EDGE,"E18.0.1.0")}),1.0]])]});
            var Q2;
            Q2=makeQuery(id+"F10.imprint","IMPRINT",FACE,{"disambiguationData":[TD([[makeQuery(id+"F10.imprint","IMPRINT",EDGE,{"derivedFrom":sQuery(id+"F10.wireOp",EDGE,"E18.1.1.0")}),1.0]])]});
            var Q3;
            Q3=makeQuery(id+"F10.imprint","IMPRINT",FACE,{"disambiguationData":[TD([[makeQuery(id+"F10.imprint","IMPRINT",EDGE,{"derivedFrom":sQuery(id+"F10.wireOp",EDGE,"E20.0.2.2")}),1.0]])]});
            var Q4;
            Q4=makeQuery(id+"F10.imprint","IMPRINT",FACE,{"disambiguationData":[TD([[makeQuery(id+"F10.imprint","IMPRINT",EDGE,{"derivedFrom":sQuery(id+"F10.wireOp",EDGE,"E18.2.1.0")}),1.0]])]});
            var Q5;
            Q5=makeQuery(id+"F10.imprint","IMPRINT",FACE,{"disambiguationData":[TD([[makeQuery(id+"F10.imprint","IMPRINT",EDGE,{"derivedFrom":sQuery(id+"F10.wireOp",EDGE,"E20.0.3.2")}),1.0]])]});
            var Q6;
            Q6=makeQuery(id+"F10.imprint","IMPRINT",FACE,{"disambiguationData":[TD([[makeQuery(id+"F10.imprint","IMPRINT",EDGE,{"derivedFrom":sQuery(id+"F10.wireOp",EDGE,"E21.0.4.3")}),1.0]])]});
            var Q7;
            Q7=makeQuery(id+"F10.imprint","IMPRINT",FACE,{"disambiguationData":[TD([[makeQuery(id+"F10.imprint","IMPRINT",EDGE,{"derivedFrom":sQuery(id+"F10.wireOp",EDGE,"E21.0.5.3")}),1.0]])]});
            var Q8;
            Q8=makeQuery(id+"F10.imprint","IMPRINT",FACE,{"disambiguationData":[TD([[makeQuery(id+"F10.imprint","IMPRINT",EDGE,{"derivedFrom":sQuery(id+"F10.wireOp",EDGE,"E21.0.6.3")}),1.0]])]});
            var Q9;
            Q9=makeQuery(id+"F10.imprint","IMPRINT",FACE,{"disambiguationData":[TD([[makeQuery(id+"F10.imprint","IMPRINT",EDGE,{"derivedFrom":sQuery(id+"F10.wireOp",EDGE,"E21.0.4.2")}),1.0]])]});
            var Q10;
            Q10=makeQuery(id+"F10.imprint","IMPRINT",FACE,{"disambiguationData":[TD([[makeQuery(id+"F10.imprint","IMPRINT",EDGE,{"derivedFrom":sQuery(id+"F10.wireOp",EDGE,"E21.0.6.4")}),1.0]])]});
            extrude(context, id + "F11", {"entities" : qUnion([Q0, Q1, Q2, Q3, Q4, Q5, Q6, Q7, Q8, Q9, Q10]), "operationType" : NewBodyOperationType.REMOVE, "endBound" : BoundingType.SYMMETRIC, "oppositeDirection" : true, "depth" : 30 * mm, "offsetDistance" : 25 * mm});
        }
        {
            var Q0;
            {var subQ0=sQuery(id+"F0.wireOp",EDGE,"E4");Q0=makeQuery(id+"F2.boolean.opBoolean","MERGE",FACE,{"derivedFrom":[makeQuery(id+"F1.opExtrude","SWEPT_FACE",FACE,{"disambiguationData":[OSD([subQ0])]}),makeQuery(id+"F2.opExtrude","SWEPT_FACE",FACE,{"disambiguationData":[OSD([subQ0])]})]});}
            var Q1;
            {var subQ0=sQuery(id+"F0.wireOp",EDGE,"E3");Q1=makeQuery(id+"F2.boolean.opBoolean","MERGE",FACE,{"derivedFrom":[makeQuery(id+"F1.opExtrude","SWEPT_FACE",FACE,{"disambiguationData":[OSD([subQ0])]}),makeQuery(id+"F2.opExtrude","SWEPT_FACE",FACE,{"disambiguationData":[OSD([subQ0])]})]});}
            var Q2;
            Q2=makeQuery(id+"F3.boolean.opBoolean","COPY",EDGE,{"derivedFrom":makeQuery(id+"F3.opExtrude","CAP_EDGE",EDGE,{"disambiguationData":[OSD([sQuery(id+"F0.wireOp",EDGE,"E11")])],"isStart":false})});
            var Q3;
            Q3=makeQuery(id+"F3.boolean.opBoolean","COPY",EDGE,{"derivedFrom":makeQuery(id+"F3.opExtrude","CAP_EDGE",EDGE,{"disambiguationData":[OSD([sQuery(id+"F0.wireOp",EDGE,"E8")])],"isStart":false})});
            var Q4;
            Q4=makeQuery(id+"F3.boolean.opBoolean","COPY",EDGE,{"derivedFrom":makeQuery(id+"F3.opExtrude","CAP_EDGE",EDGE,{"disambiguationData":[OSD([sQuery(id+"F0.wireOp",EDGE,"E9")])],"isStart":false})});
            var Q5;
            Q5=makeQuery(id+"F3.boolean.opBoolean","COPY",EDGE,{"derivedFrom":makeQuery(id+"F3.opExtrude","CAP_EDGE",EDGE,{"disambiguationData":[OSD([sQuery(id+"F0.wireOp",EDGE,"E10")])],"isStart":false})});
            var Q6;
            Q6=makeQuery(id+"F3.boolean.opBoolean","COPY",EDGE,{"derivedFrom":makeQuery(id+"F3.opExtrude","CAP_EDGE",EDGE,{"disambiguationData":[OSD([sQuery(id+"F0.wireOp",EDGE,"E8")])],"isStart":true})});
            var Q7;
            Q7=makeQuery(id+"F3.boolean.opBoolean","COPY",EDGE,{"derivedFrom":makeQuery(id+"F3.opExtrude","CAP_EDGE",EDGE,{"disambiguationData":[OSD([sQuery(id+"F0.wireOp",EDGE,"E11")])],"isStart":true})});
            var Q8;
            Q8=makeQuery(id+"F3.boolean.opBoolean","COPY",EDGE,{"derivedFrom":makeQuery(id+"F3.opExtrude","CAP_EDGE",EDGE,{"disambiguationData":[OSD([sQuery(id+"F0.wireOp",EDGE,"E10")])],"isStart":true})});
            var Q9;
            Q9=makeQuery(id+"F3.boolean.opBoolean","COPY",EDGE,{"derivedFrom":makeQuery(id+"F3.opExtrude","CAP_EDGE",EDGE,{"disambiguationData":[OSD([sQuery(id+"F0.wireOp",EDGE,"E9")])],"isStart":true})});
            chamfer(context, id + "F12", {"entities" : qUnion([Q0, Q1, Q2, Q3, Q4, Q5, Q6, Q7, Q8, Q9]), "width" : 2 * mm, "tangentPropagation" : true});
        }
    });
